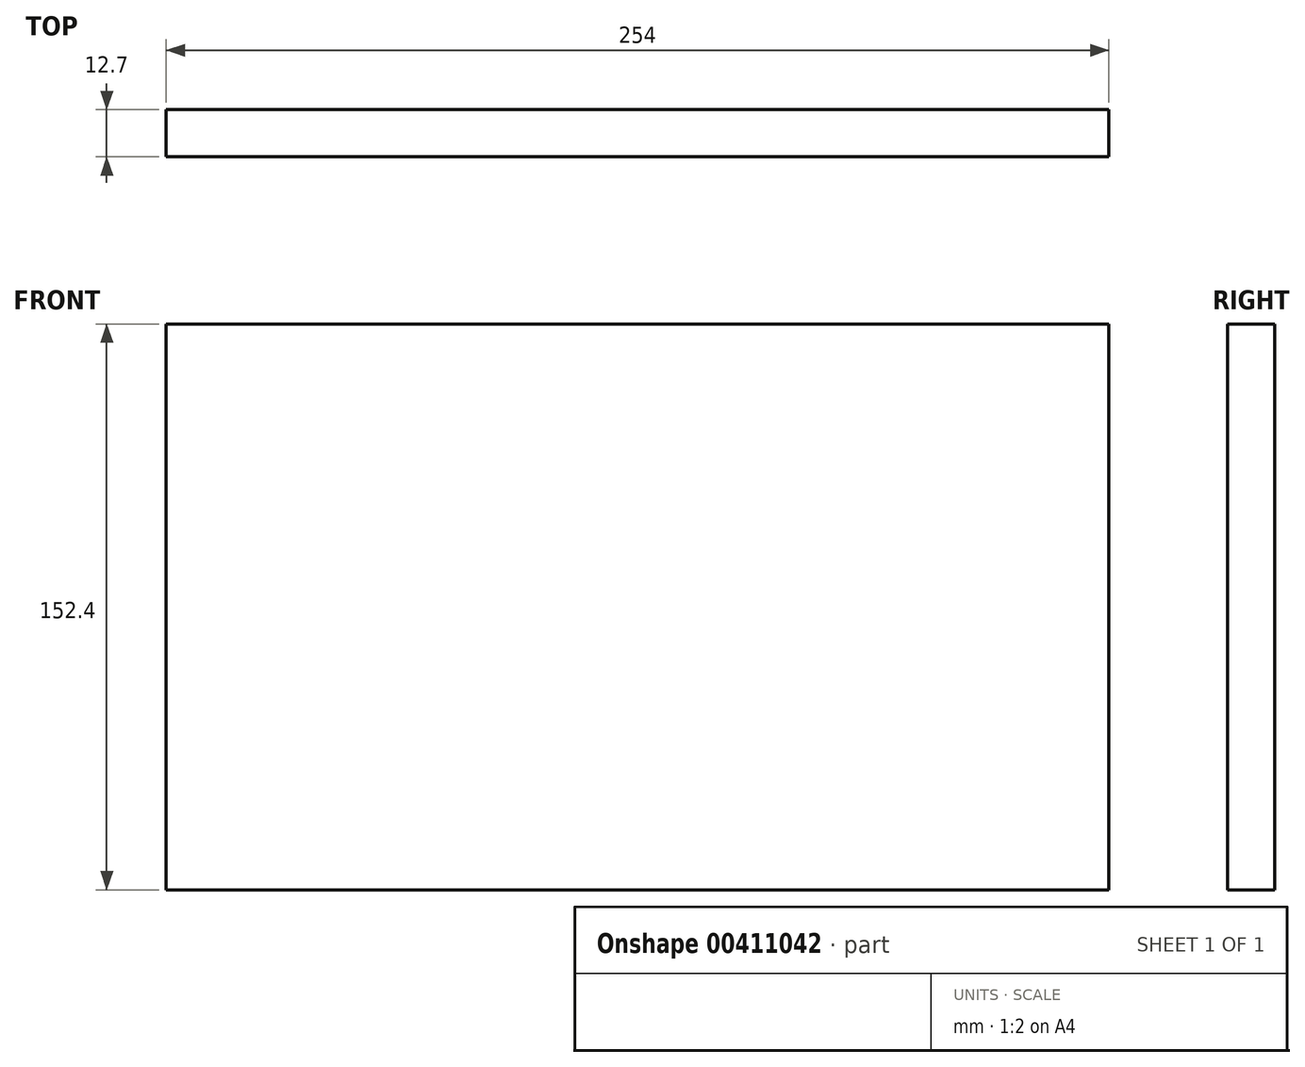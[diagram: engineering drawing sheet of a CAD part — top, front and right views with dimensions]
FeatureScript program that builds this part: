
annotation { "Feature Type Name" : "Feature", "Feature Type Description" : "" }
export const myFeature = defineFeature(function(context is Context, id is Id, definition is map)
    precondition{}
    {
        {
            var Q0;
            Q0=qCreatedBy(makeId("Front.planeOp"),FACE);
            var sketch = newSketch(context, id + "F0", { "sketchPlane" : qUnion([Q0])});
            skLineSegment(sketch, "E0.bottom", {"start": v(254, 0) * mm, "end": v(0, 0) * mm});
            skLineSegment(sketch, "E0.top", {"start": v(254, 152.4) * mm, "end": v(0, 152.4) * mm});
            skLineSegment(sketch, "E0.left", {"start": v(254, 0) * mm, "end": v(254, 152.4) * mm});
            skLineSegment(sketch, "E0.right", {"start": v(0, 0) * mm, "end": v(0, 152.4) * mm});
            skSolve(sketch);
        }
        {
            var Q0;
            Q0 = qSketchRegion(id + "F0", true);
            extrude(context, id + "F1", {"entities" : qUnion([Q0]), "oppositeDirection" : true, "depth" : 12.7 * mm});
        }
    });
